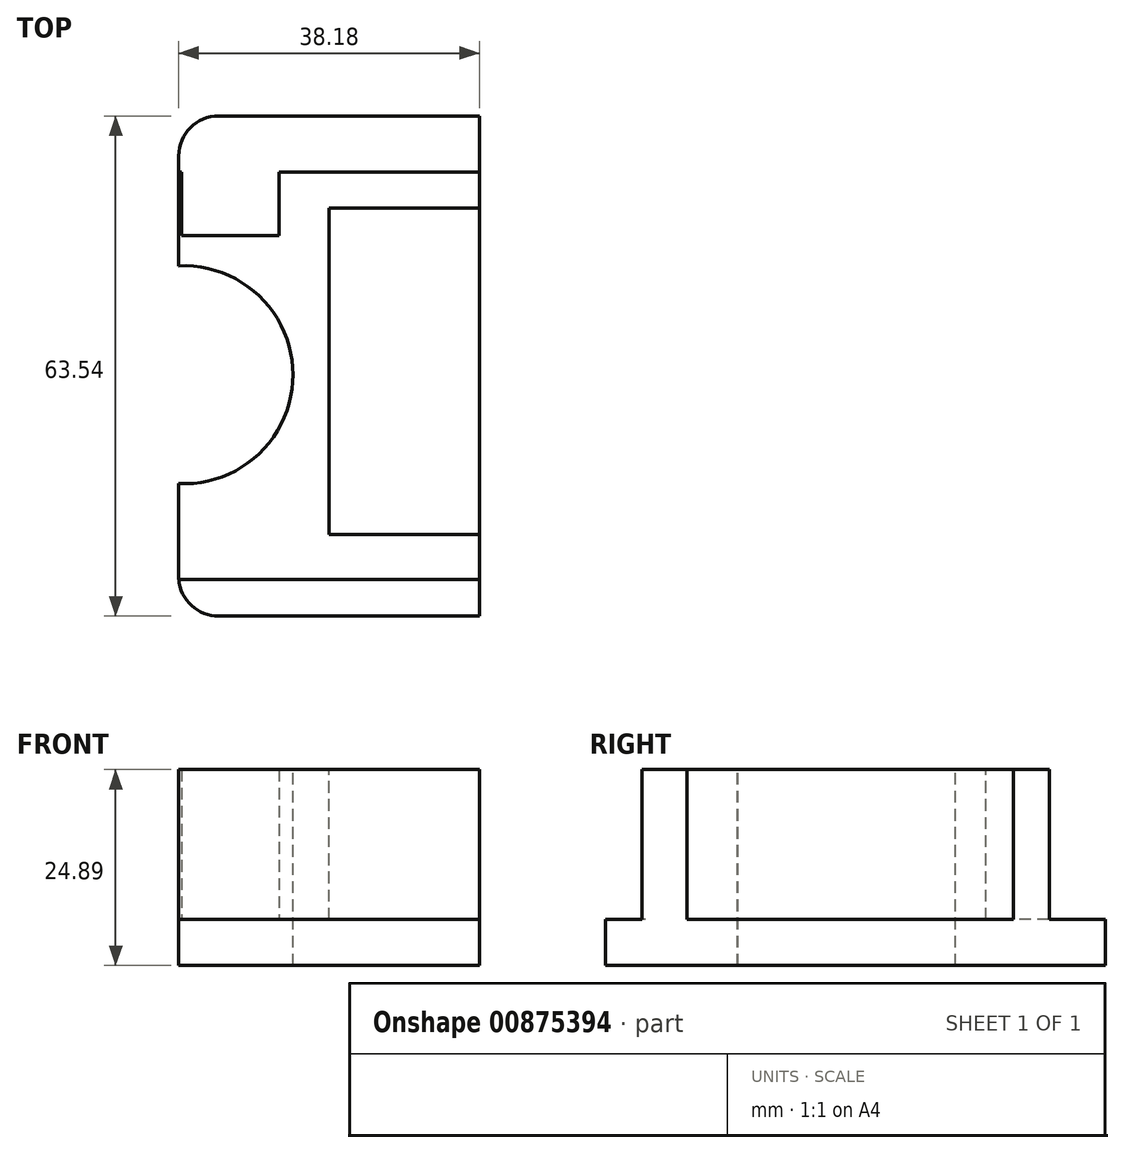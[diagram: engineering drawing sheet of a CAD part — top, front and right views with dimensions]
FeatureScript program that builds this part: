
annotation { "Feature Type Name" : "Feature", "Feature Type Description" : "" }
export const myFeature = defineFeature(function(context is Context, id is Id, definition is map)
    precondition{}
    {
        {
            var Q0;
            Q0=qCreatedBy(makeId("Top.planeOp"),FACE);
            var sketch = newSketch(context, id + "F0", { "sketchPlane" : qUnion([Q0])});
            skLineSegment(sketch, "E0.bottom", {"start": v(-59.02, 55.96) * mm, "end": v(-20.84, 55.96) * mm});
            skLineSegment(sketch, "E0.top", {"start": v(-59.02, -7.58) * mm, "end": v(-20.84, -7.58) * mm});
            skLineSegment(sketch, "E0.left", {"start": v(-59.02, 55.96) * mm, "end": v(-59.02, -7.58) * mm});
            skLineSegment(sketch, "E0.right", {"start": v(-20.84, 55.96) * mm, "end": v(-20.84, -7.58) * mm});
            skSolve(sketch);
        }
        {
            var Q0;
            Q0 = qSketchRegion(id + "F0", true);
            extrude(context, id + "F1", {"entities" : qUnion([Q0]), "depth" : 5.84 * mm, "offsetDistance" : 25.4 * mm});
        }
        {
            var Q0;
            Q0=makeQuery(id+"F1.opExtrude","SWEPT_EDGE",EDGE,{"disambiguationData":[OSD([sQuery(id+"F0.wireOp",EDGE,"E0.bottom"),sQuery(id+"F0.wireOp",EDGE,"E0.left")])]});
            var Q1;
            Q1=makeQuery(id+"F1.opExtrude","SWEPT_EDGE",EDGE,{"disambiguationData":[OSD([sQuery(id+"F0.wireOp",EDGE,"E0.top"),sQuery(id+"F0.wireOp",EDGE,"E0.left")])]});
            fillet(context, id + "F2", {"entities" : qUnion([Q0, Q1]), "radius" : 5.08 * mm, "tangentPropagation" : true, "allowEdgeOverflow" : false});
        }
        {
            var Q0;
            Q0=makeQuery(id+"F1.opExtrude","CAP_FACE",FACE,{"disambiguationData":[OSD([sQuery(id+"F0.wireOp",EDGE,"E0.bottom"),sQuery(id+"F0.wireOp",EDGE,"E0.top"),sQuery(id+"F0.wireOp",EDGE,"E0.left"),sQuery(id+"F0.wireOp",EDGE,"E0.right")])],"isStart":false});
            var sketch = newSketch(context, id + "F3", { "sketchPlane" : qUnion([Q0])});
            skLineSegment(sketch, "E1.bottom", {"start": v(-20.84, 48.8) * mm, "end": v(-59.02, 48.8) * mm});
            skLineSegment(sketch, "E1.top", {"start": v(-20.84, -2.9) * mm, "end": v(-59.02, -2.9) * mm});
            skLineSegment(sketch, "E1.left", {"start": v(-20.84, 48.8) * mm, "end": v(-20.84, -2.9) * mm});
            skLineSegment(sketch, "E1.right", {"start": v(-59.02, 48.8) * mm, "end": v(-59.02, -2.9) * mm});
            skPoint(sketch, "E1.middle", {"position": v(-39.93, 22.95) * mm});
            skSolve(sketch);
        }
        {
            var Q0;
            Q0 = qSketchRegion(id + "F3", true);
            extrude(context, id + "F4", {"entities" : qUnion([Q0]), "operationType" : NewBodyOperationType.ADD, "depth" : 19.05 * mm, "offsetDistance" : 25.4 * mm});
        }
        {
            var Q0;
            Q0=makeQuery(id+"F4.opExtrude","CAP_FACE",FACE,{"disambiguationData":[OSD([sQuery(id+"F3.wireOp",EDGE,"E1.bottom"),sQuery(id+"F3.wireOp",EDGE,"E1.top"),sQuery(id+"F3.wireOp",EDGE,"E1.left"),sQuery(id+"F3.wireOp",EDGE,"E1.right")])],"isStart":false});
            var sketch = newSketch(context, id + "F5", { "sketchPlane" : qUnion([Q0])});
            skLineSegment(sketch, "E2.bottom", {"start": v(-20.84, 44.28) * mm, "end": v(-39.93, 44.28) * mm});
            skLineSegment(sketch, "E2.top", {"start": v(-20.84, 2.8) * mm, "end": v(-39.93, 2.8) * mm});
            skLineSegment(sketch, "E2.left", {"start": v(-20.84, 44.28) * mm, "end": v(-20.84, 0) * mm});
            skLineSegment(sketch, "E2.right", {"start": v(-39.93, 44.28) * mm, "end": v(-39.93, 0) * mm});
            skPoint(sketch, "E2.middle", {"position": v(-30.39, 22.14) * mm});
            skSolve(sketch);
        }
        {
            var Q0;
            Q0 = qSketchRegion(id + "F5", true);
            extrude(context, id + "F6", {"entities" : qUnion([Q0]), "operationType" : NewBodyOperationType.REMOVE, "oppositeDirection" : true, "depth" : 19.05 * mm, "offsetDistance" : 25.4 * mm});
        }
        {
            var Q0;
            Q0=makeQuery(id+"F4.opExtrude","CAP_FACE",FACE,{"disambiguationData":[OSD([sQuery(id+"F3.wireOp",EDGE,"E1.bottom"),sQuery(id+"F3.wireOp",EDGE,"E1.top"),sQuery(id+"F3.wireOp",EDGE,"E1.left"),sQuery(id+"F3.wireOp",EDGE,"E1.right")])],"isStart":false});
            var sketch = newSketch(context, id + "F7", { "sketchPlane" : qUnion([Q0])});
            skSolve(sketch);
        }
        {
            var Q0;
            {var subQ3=sQuery(id+"F3.wireOp",EDGE,"E1.bottom");Q0=makeQuery(id+"F7.imprint","IMPRINT",FACE,{"disambiguationData":[TD([[makeQuery(id+"F7.imprint","IMPRINT",EDGE,{"derivedFrom":makeQuery(id+"F4.opExtrude","CAP_EDGE",EDGE,{"disambiguationData":[OSD([subQ3])],"isStart":false})}),1.0]])]});}
            var sketch = newSketch(context, id + "F8", { "sketchPlane" : qUnion([Q0])});
            skCircle(sketch, "E3", {"center": v(-58.36, 23.08) * mm, "radius": 13.84 * mm});
            skSolve(sketch);
        }
        {
            var Q0;
            Q0 = qSketchRegion(id + "F8", true);
            extrude(context, id + "F9", {"entities" : qUnion([Q0]), "operationType" : NewBodyOperationType.REMOVE, "oppositeDirection" : true, "depth" : 25.4 * mm, "offsetDistance" : 25.4 * mm});
        }
        {
            var Q0;
            {var subQ3=sQuery(id+"F3.wireOp",EDGE,"E1.bottom");Q0=makeQuery(id+"F7.imprint","IMPRINT",FACE,{"disambiguationData":[TD([[makeQuery(id+"F7.imprint","IMPRINT",EDGE,{"derivedFrom":makeQuery(id+"F4.opExtrude","CAP_EDGE",EDGE,{"disambiguationData":[OSD([subQ3])],"isStart":false})}),1.0]])]});}
            var sketch = newSketch(context, id + "F10", { "sketchPlane" : qUnion([Q0])});
            skLineSegment(sketch, "E4.bottom", {"start": v(-46.3, 48.93) * mm, "end": v(-58.68, 48.93) * mm});
            skLineSegment(sketch, "E4.top", {"start": v(-46.3, 40.77) * mm, "end": v(-58.68, 40.77) * mm});
            skLineSegment(sketch, "E4.left", {"start": v(-46.3, 48.93) * mm, "end": v(-46.3, 40.77) * mm});
            skLineSegment(sketch, "E4.right", {"start": v(-58.68, 48.93) * mm, "end": v(-58.68, 40.77) * mm});
            skSolve(sketch);
        }
        {
            var Q0;
            Q0 = qSketchRegion(id + "F10", true);
            extrude(context, id + "F11", {"entities" : qUnion([Q0]), "operationType" : NewBodyOperationType.REMOVE, "oppositeDirection" : true, "depth" : 19.05 * mm, "offsetDistance" : 25.4 * mm});
        }
    });
